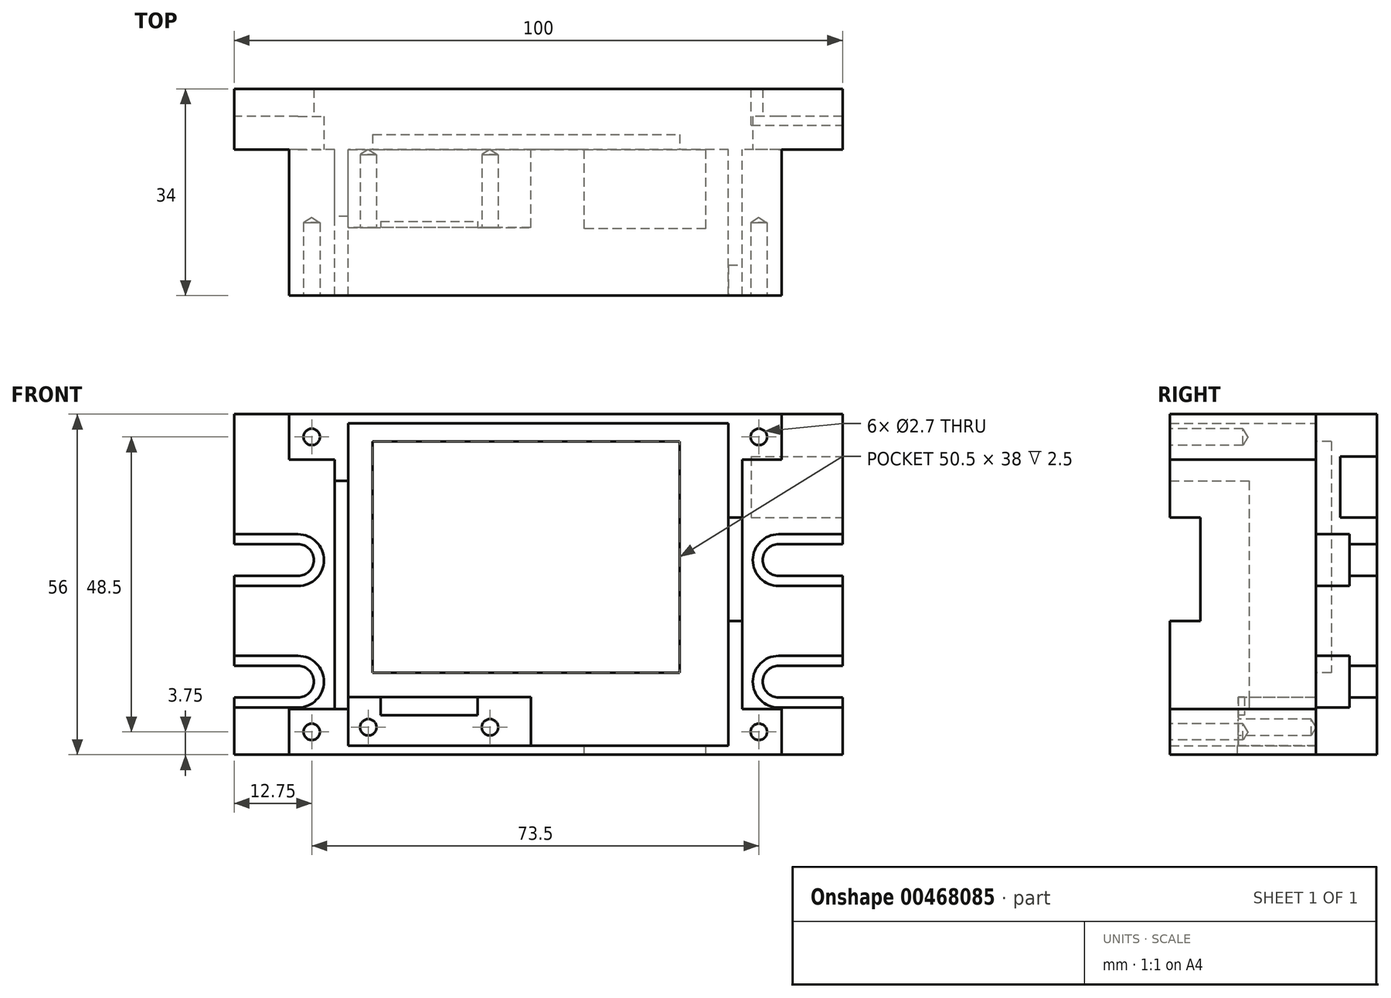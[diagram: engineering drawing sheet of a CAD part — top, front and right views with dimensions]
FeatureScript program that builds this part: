
annotation { "Feature Type Name" : "Feature", "Feature Type Description" : "" }
export const myFeature = defineFeature(function(context is Context, id is Id, definition is map)
    precondition{}
    {
        {
            var Q0;
            Q0=qCreatedBy(makeId("Front.planeOp"),FACE);
            var sketch = newSketch(context, id + "F0", { "sketchPlane" : qUnion([Q0])});
            skLineSegment(sketch, "E0", {"start": v(-65, 0) * mm, "end": v(-65, 5) * mm});
            skLineSegment(sketch, "E1", {"start": v(-65, 5) * mm, "end": v(-50, 5) * mm});
            skLineSegment(sketch, "E2", {"start": v(-50, 5) * mm, "end": v(-50, 61) * mm});
            skLineSegment(sketch, "E3", {"start": v(-50, 61) * mm, "end": v(50, 61) * mm});
            skLineSegment(sketch, "E4", {"start": v(50, 61) * mm, "end": v(50, 5) * mm});
            skLineSegment(sketch, "E5", {"start": v(50, 5) * mm, "end": v(65, 5) * mm});
            skLineSegment(sketch, "E6", {"start": v(65, 5) * mm, "end": v(65, 0) * mm});
            skLineSegment(sketch, "E7", {"start": v(65, 0) * mm, "end": v(-65, 0) * mm});
            skLineSegment(sketch, "E8", {"start": v(-66.2, 33) * mm, "end": v(67.97, 33) * mm, "construction": true});
            skLineSegment(sketch, "E9.bottom", {"start": v(-38, 45.5) * mm, "end": v(38, 45.5) * mm, "construction": true});
            skLineSegment(sketch, "E9.top", {"start": v(-38, 20.5) * mm, "end": v(38, 20.5) * mm, "construction": true});
            skLineSegment(sketch, "E9.left", {"start": v(-38, 45.5) * mm, "end": v(-38, 20.5) * mm, "construction": true});
            skLineSegment(sketch, "E9.right", {"start": v(38, 45.5) * mm, "end": v(38, 20.5) * mm, "construction": true});
            skSolve(sketch);
        }
        {
            var Q0;
            Q0=qSketchRegion(id+"F0",true);
            extrude(context, id + "F1", {"entities" : qUnion([Q0]), "depth" : 12 * mm});
        }
        {
            var Q0;
            Q0=makeQuery(id+"F1.opExtrude","SWEPT_FACE",FACE,{"disambiguationData":[OSD([sQuery(id+"F0.wireOp",EDGE,"E7")])]});
            var sketch = newSketch(context, id + "F2", { "sketchPlane" : qUnion([Q0])});
            skLineSegment(sketch, "E10", {"start": v(-65, 6) * mm, "end": v(65, 6) * mm, "construction": true});
            skArc(sketch, "E11", {"start": v(-63, 2.65) * mm, "mid": v(-59.65, 6) * mm, "end": v(-63, 9.35) * mm});
            skArc(sketch, "E12", {"start": v(63, 9.35) * mm, "mid": v(59.65, 6) * mm, "end": v(63, 2.65) * mm});
            skLineSegment(sketch, "E13", {"start": v(-63, 9.35) * mm, "end": v(-65, 9.35) * mm});
            skLineSegment(sketch, "E14", {"start": v(-63, 2.65) * mm, "end": v(-65, 2.65) * mm});
            skLineSegment(sketch, "E15", {"start": v(-65, 9.35) * mm, "end": v(-65, 2.65) * mm});
            skLineSegment(sketch, "E16", {"start": v(63, 9.35) * mm, "end": v(65, 9.35) * mm});
            skLineSegment(sketch, "E17", {"start": v(63, 2.65) * mm, "end": v(65, 2.65) * mm});
            skLineSegment(sketch, "E18", {"start": v(65, 2.65) * mm, "end": v(65, 9.35) * mm});
            skSolve(sketch);
        }
        {
            var Q0;
            Q0=qSketchRegion(id+"F2",true);
            extrude(context, id + "F3", {"entities" : qUnion([Q0]), "operationType" : NewBodyOperationType.REMOVE, "endBound" : BoundingType.UP_TO_NEXT, "oppositeDirection" : true, "depth" : 25 * mm});
        }
        {
            var Q0;
            Q0=makeQuery(id+"F1.opExtrude","CAP_FACE",FACE,{"disambiguationData":[OSD([sQuery(id+"F0.wireOp",EDGE,"E0"),sQuery(id+"F0.wireOp",EDGE,"E1"),sQuery(id+"F0.wireOp",EDGE,"E2"),sQuery(id+"F0.wireOp",EDGE,"E3"),sQuery(id+"F0.wireOp",EDGE,"E4"),sQuery(id+"F0.wireOp",EDGE,"E5"),sQuery(id+"F0.wireOp",EDGE,"E6"),sQuery(id+"F0.wireOp",EDGE,"E7"),sQuery(id+"F0.wireOp",EDGE,"1FfViyJT-DljK-amIZ-o1TR-3zgzdxAZsou7"),sQuery(id+"F0.wireOp",EDGE,"gixynyuw-ZIOC-nsWz-2FFo-MeVdqOtkgReW"),sQuery(id+"F0.wireOp",EDGE,"ZI2TBTUG-xJa5-HuRL-xrIj-cNeYduNTSZAt"),sQuery(id+"F0.wireOp",EDGE,"0vhO7cF5-ESn1-LKnd-qrl0-O6yNl9EkdQ3n")])],"isStart":true});
            var sketch = newSketch(context, id + "F4", { "sketchPlane" : qUnion([Q0])});
            skLineSegment(sketch, "E19.bottom", {"start": v(50, 5) * mm, "end": v(-50, 5) * mm});
            skLineSegment(sketch, "E19.top", {"start": v(50, 61) * mm, "end": v(-50, 61) * mm});
            skLineSegment(sketch, "E19.left", {"start": v(50, 5) * mm, "end": v(50, 61) * mm});
            skLineSegment(sketch, "E19.right", {"start": v(-50, 5) * mm, "end": v(-50, 61) * mm});
            skSolve(sketch);
        }
        {
            var Q0;
            Q0=qSketchRegion(id+"F4",true);
            extrude(context, id + "F5", {"entities" : qUnion([Q0]), "operationType" : NewBodyOperationType.REMOVE, "oppositeDirection" : true, "depth" : 2 * mm});
        }
        {
            var Q0;
            Q0=makeQuery(id+"F1.opExtrude","CAP_FACE",FACE,{"disambiguationData":[OSD([sQuery(id+"F0.wireOp",EDGE,"E0"),sQuery(id+"F0.wireOp",EDGE,"E1"),sQuery(id+"F0.wireOp",EDGE,"E2"),sQuery(id+"F0.wireOp",EDGE,"E3"),sQuery(id+"F0.wireOp",EDGE,"E4"),sQuery(id+"F0.wireOp",EDGE,"E5"),sQuery(id+"F0.wireOp",EDGE,"E6"),sQuery(id+"F0.wireOp",EDGE,"E7"),sQuery(id+"F0.wireOp",EDGE,"1FfViyJT-DljK-amIZ-o1TR-3zgzdxAZsou7"),sQuery(id+"F0.wireOp",EDGE,"gixynyuw-ZIOC-nsWz-2FFo-MeVdqOtkgReW"),sQuery(id+"F0.wireOp",EDGE,"ZI2TBTUG-xJa5-HuRL-xrIj-cNeYduNTSZAt"),sQuery(id+"F0.wireOp",EDGE,"0vhO7cF5-ESn1-LKnd-qrl0-O6yNl9EkdQ3n")])],"isStart":true});
            var sketch = newSketch(context, id + "F6", { "sketchPlane" : qUnion([Q0])});
            skLineSegment(sketch, "E20.bottom", {"start": v(65, 5) * mm, "end": v(-65, 5) * mm});
            skLineSegment(sketch, "E20.top", {"start": v(65, 0) * mm, "end": v(-65, 0) * mm});
            skLineSegment(sketch, "E20.left", {"start": v(65, 5) * mm, "end": v(65, 0) * mm});
            skLineSegment(sketch, "E20.right", {"start": v(-65, 5) * mm, "end": v(-65, 0) * mm});
            skSolve(sketch);
        }
        {
            var Q0;
            Q0=qSketchRegion(id+"F6",true);
            extrude(context, id + "F7", {"entities" : qUnion([Q0]), "operationType" : NewBodyOperationType.REMOVE, "endBound" : BoundingType.THROUGH_ALL, "oppositeDirection" : true, "depth" : 25 * mm});
        }
        {
            var Q0;
            Q0=makeQuery(id+"F1.opExtrude","CAP_FACE",FACE,{"disambiguationData":[OSD([sQuery(id+"F0.wireOp",EDGE,"E0"),sQuery(id+"F0.wireOp",EDGE,"E1"),sQuery(id+"F0.wireOp",EDGE,"E2"),sQuery(id+"F0.wireOp",EDGE,"E3"),sQuery(id+"F0.wireOp",EDGE,"E4"),sQuery(id+"F0.wireOp",EDGE,"E5"),sQuery(id+"F0.wireOp",EDGE,"E6"),sQuery(id+"F0.wireOp",EDGE,"E7"),sQuery(id+"F0.wireOp",EDGE,"1FfViyJT-DljK-amIZ-o1TR-3zgzdxAZsou7"),sQuery(id+"F0.wireOp",EDGE,"gixynyuw-ZIOC-nsWz-2FFo-MeVdqOtkgReW"),sQuery(id+"F0.wireOp",EDGE,"ZI2TBTUG-xJa5-HuRL-xrIj-cNeYduNTSZAt"),sQuery(id+"F0.wireOp",EDGE,"0vhO7cF5-ESn1-LKnd-qrl0-O6yNl9EkdQ3n")])],"isStart":false});
            var sketch = newSketch(context, id + "F8", { "sketchPlane" : qUnion([Q0])});
            skLineSegment(sketch, "E21.bottom", {"start": v(-52.5, 6) * mm, "end": v(52.5, 6) * mm, "construction": true});
            skLineSegment(sketch, "E21.top", {"start": v(-52.5, 60) * mm, "end": v(52.5, 60) * mm, "construction": true});
            skLineSegment(sketch, "E21.left", {"start": v(-52.5, 6) * mm, "end": v(-52.5, 60) * mm, "construction": true});
            skLineSegment(sketch, "E21.right", {"start": v(52.5, 6) * mm, "end": v(52.5, 60) * mm, "construction": true});
            skLineSegment(sketch, "E22", {"start": v(-65.76, 33) * mm, "end": v(79.5, 33) * mm, "construction": true});
            skArc(sketch, "E23.MirrorCS", {"start": v(-39.5, 39.6) * mm, "mid": v(-36.9, 37) * mm, "end": v(-39.5, 34.4) * mm});
            skLineSegment(sketch, "E24", {"start": v(0, 73.09) * mm, "end": v(0, -19.71) * mm, "construction": true});
            skPoint(sketch, "E24.startSnap0", {"position": v(0, 61) * mm});
            skLineSegment(sketch, "E25", {"start": v(-39.5, 39.6) * mm, "end": v(-50, 39.6) * mm});
            skLineSegment(sketch, "E26", {"start": v(-50, 39.6) * mm, "end": v(-50, 34.4) * mm});
            skLineSegment(sketch, "E27", {"start": v(-50, 34.4) * mm, "end": v(-39.5, 34.4) * mm});
            skLineSegment(sketch, "E28.0.1.0", {"start": v(-50, 19.6) * mm, "end": v(-50, 14.4) * mm});
            skLineSegment(sketch, "E28.0.1.1", {"start": v(-50, 14.4) * mm, "end": v(-39.5, 14.4) * mm});
            skLineSegment(sketch, "E28.0.1.2", {"start": v(-39.5, 19.6) * mm, "end": v(-50, 19.6) * mm});
            skArc(sketch, "E28.0.1.3", {"start": v(-39.5, 19.6) * mm, "mid": v(-36.9, 17) * mm, "end": v(-39.5, 14.4) * mm});
            skLineSegment(sketch, "E28.direction1", {"start": v(-50, 34.4) * mm, "end": v(-25, 34.4) * mm, "construction": true});
            skLineSegment(sketch, "E28.direction2", {"start": v(-50, 34.4) * mm, "end": v(-50, 14.4) * mm, "construction": true});
            skArc(sketch, "E29.MirrorCS", {"start": v(39.5, 39.6) * mm, "mid": v(36.9, 37) * mm, "end": v(39.5, 34.4) * mm});
            skLineSegment(sketch, "E30.MirrorCS", {"start": v(50, 39.6) * mm, "end": v(50, 34.4) * mm});
            skLineSegment(sketch, "E31.MirrorCS", {"start": v(50, 19.6) * mm, "end": v(50, 14.4) * mm});
            skArc(sketch, "E32.MirrorCS", {"start": v(39.5, 19.6) * mm, "mid": v(36.9, 17) * mm, "end": v(39.5, 14.4) * mm});
            skLineSegment(sketch, "E33.MirrorCS", {"start": v(50, 34.4) * mm, "end": v(39.5, 34.4) * mm});
            skLineSegment(sketch, "E34.MirrorCS", {"start": v(50, 34.4) * mm, "end": v(50, 14.4) * mm, "construction": true});
            skLineSegment(sketch, "E35.MirrorCS", {"start": v(50, 34.4) * mm, "end": v(25, 34.4) * mm, "construction": true});
            skLineSegment(sketch, "E36.MirrorCS", {"start": v(39.5, 39.6) * mm, "end": v(50, 39.6) * mm});
            skLineSegment(sketch, "E37.MirrorCS", {"start": v(50, 14.4) * mm, "end": v(39.5, 14.4) * mm});
            skLineSegment(sketch, "E38.MirrorCS", {"start": v(39.5, 19.6) * mm, "end": v(50, 19.6) * mm});
            skSolve(sketch);
        }
        {
            var Q0;
            Q0=qSketchRegion(id+"F8",true);
            extrude(context, id + "F9", {"entities" : qUnion([Q0]), "operationType" : NewBodyOperationType.REMOVE, "endBound" : BoundingType.THROUGH_ALL, "oppositeDirection" : true, "depth" : 25 * mm});
        }
        {
            var Q0;
            Q0=makeQuery(id+"F1.opExtrude","CAP_FACE",FACE,{"disambiguationData":[OSD([sQuery(id+"F0.wireOp",EDGE,"E0"),sQuery(id+"F0.wireOp",EDGE,"E1"),sQuery(id+"F0.wireOp",EDGE,"E2"),sQuery(id+"F0.wireOp",EDGE,"E3"),sQuery(id+"F0.wireOp",EDGE,"E4"),sQuery(id+"F0.wireOp",EDGE,"E5"),sQuery(id+"F0.wireOp",EDGE,"E6"),sQuery(id+"F0.wireOp",EDGE,"E7"),sQuery(id+"F0.wireOp",EDGE,"1FfViyJT-DljK-amIZ-o1TR-3zgzdxAZsou7"),sQuery(id+"F0.wireOp",EDGE,"gixynyuw-ZIOC-nsWz-2FFo-MeVdqOtkgReW"),sQuery(id+"F0.wireOp",EDGE,"ZI2TBTUG-xJa5-HuRL-xrIj-cNeYduNTSZAt"),sQuery(id+"F0.wireOp",EDGE,"0vhO7cF5-ESn1-LKnd-qrl0-O6yNl9EkdQ3n")])],"isStart":false});
            var sketch = newSketch(context, id + "F10", { "sketchPlane" : qUnion([Q0])});
            skArc(sketch, "E39", {"start": v(-39.5, 32.75) * mm, "mid": v(-35.25, 37) * mm, "end": v(-39.5, 41.25) * mm});
            skLineSegment(sketch, "E40", {"start": v(-39.5, 41.25) * mm, "end": v(-50, 41.25) * mm});
            skLineSegment(sketch, "E41", {"start": v(-39.5, 32.75) * mm, "end": v(-50, 32.75) * mm});
            skLineSegment(sketch, "E42", {"start": v(0, 67.71) * mm, "end": v(0, -2.74) * mm, "construction": true});
            skPoint(sketch, "E42.startSnap0", {"position": v(0, 61) * mm});
            skLineSegment(sketch, "E43.0.1.0", {"start": v(-39.5, 12.75) * mm, "end": v(-50, 12.75) * mm});
            skLineSegment(sketch, "E43.0.1.1", {"start": v(-39.5, 21.25) * mm, "end": v(-50, 21.25) * mm});
            skArc(sketch, "E43.0.1.2", {"start": v(-39.5, 12.75) * mm, "mid": v(-35.25, 17) * mm, "end": v(-39.5, 21.25) * mm});
            skLineSegment(sketch, "E43.direction1", {"start": v(-50, 32.75) * mm, "end": v(-25, 32.75) * mm, "construction": true});
            skLineSegment(sketch, "E43.direction2", {"start": v(-50, 32.75) * mm, "end": v(-50, 12.75) * mm, "construction": true});
            skLineSegment(sketch, "E44.MirrorCS", {"start": v(39.5, 32.75) * mm, "end": v(50, 32.75) * mm});
            skLineSegment(sketch, "E45.MirrorCS", {"start": v(50, 32.75) * mm, "end": v(50, 12.75) * mm, "construction": true});
            skLineSegment(sketch, "E46.MirrorCS", {"start": v(39.5, 21.25) * mm, "end": v(50, 21.25) * mm});
            skLineSegment(sketch, "E47.MirrorCS", {"start": v(39.5, 12.75) * mm, "end": v(50, 12.75) * mm});
            skArc(sketch, "E48.MirrorCS", {"start": v(39.5, 12.75) * mm, "mid": v(35.25, 17) * mm, "end": v(39.5, 21.25) * mm});
            skArc(sketch, "E49.MirrorCS", {"start": v(39.5, 32.75) * mm, "mid": v(35.25, 37) * mm, "end": v(39.5, 41.25) * mm});
            skLineSegment(sketch, "E50.MirrorCS", {"start": v(39.5, 41.25) * mm, "end": v(50, 41.25) * mm});
            skLineSegment(sketch, "E51.MirrorCS", {"start": v(50, 32.75) * mm, "end": v(25, 32.75) * mm, "construction": true});
            skSolve(sketch);
        }
        {
            var Q0;
            Q0=makeQuery(id+"F10.imprint","IMPRINT",FACE,{"disambiguationData":[TD([[makeQuery(id+"F10.imprint","IMPRINT",EDGE,{"derivedFrom":sQuery(id+"F10.wireOp",EDGE,"E39")}),1.0]])]});
            var Q1;
            {var subQ3=sQuery(id+"F10.wireOp",EDGE,"E43.0.1.0");Q1=makeQuery(id+"F10.imprint","IMPRINT",FACE,{"disambiguationData":[TD([[makeQuery(id+"F10.imprint","IMPRINT",EDGE,{"derivedFrom":subQ3}),-1.0]])]});}
            var Q2;
            {var subQ3=sQuery(id+"F10.wireOp",EDGE,"E44.MirrorCS");Q2=makeQuery(id+"F10.imprint","IMPRINT",FACE,{"disambiguationData":[TD([[makeQuery(id+"F10.imprint","IMPRINT",EDGE,{"derivedFrom":subQ3}),1.0]])]});}
            var Q3;
            {var subQ1=sQuery(id+"F10.wireOp",EDGE,"E46.MirrorCS");Q3=makeQuery(id+"F10.imprint","IMPRINT",FACE,{"disambiguationData":[TD([[makeQuery(id+"F10.imprint","IMPRINT",EDGE,{"derivedFrom":subQ1}),-1.0]])]});}
            extrude(context, id + "F11", {"entities" : qUnion([Q0, Q1, Q2, Q3]), "operationType" : NewBodyOperationType.REMOVE, "oppositeDirection" : true, "depth" : 5.5 * mm});
        }
        {
            var Q0;
            Q0=makeQuery(id+"F1.opExtrude","CAP_FACE",FACE,{"disambiguationData":[OSD([sQuery(id+"F0.wireOp",EDGE,"E0"),sQuery(id+"F0.wireOp",EDGE,"E1"),sQuery(id+"F0.wireOp",EDGE,"E2"),sQuery(id+"F0.wireOp",EDGE,"E3"),sQuery(id+"F0.wireOp",EDGE,"E4"),sQuery(id+"F0.wireOp",EDGE,"E5"),sQuery(id+"F0.wireOp",EDGE,"E6"),sQuery(id+"F0.wireOp",EDGE,"E7"),sQuery(id+"F0.wireOp",EDGE,"1FfViyJT-DljK-amIZ-o1TR-3zgzdxAZsou7"),sQuery(id+"F0.wireOp",EDGE,"gixynyuw-ZIOC-nsWz-2FFo-MeVdqOtkgReW"),sQuery(id+"F0.wireOp",EDGE,"ZI2TBTUG-xJa5-HuRL-xrIj-cNeYduNTSZAt"),sQuery(id+"F0.wireOp",EDGE,"0vhO7cF5-ESn1-LKnd-qrl0-O6yNl9EkdQ3n")])],"isStart":false});
            var sketch = newSketch(context, id + "F12", { "sketchPlane" : qUnion([Q0])});
            skLineSegment(sketch, "E52", {"start": v(-67.67, 33) * mm, "end": v(65.75, 33) * mm, "construction": true});
            skPoint(sketch, "E52.startSnap0", {"position": v(-50, 33) * mm});
            skLineSegment(sketch, "E53", {"start": v(0, 70.32) * mm, "end": v(0, -7.36) * mm, "construction": true});
            skPoint(sketch, "E53.startSnap0", {"position": v(0, 61) * mm});
            skLineSegment(sketch, "E54.bottom", {"start": v(31.25, 59.5) * mm, "end": v(-31.25, 59.5) * mm});
            skLineSegment(sketch, "E54.top", {"start": v(31.25, 6.5) * mm, "end": v(-31.25, 6.5) * mm});
            skLineSegment(sketch, "E54.left", {"start": v(31.25, 59.5) * mm, "end": v(31.25, 6.5) * mm});
            skLineSegment(sketch, "E54.right", {"start": v(-31.25, 59.5) * mm, "end": v(-31.25, 6.5) * mm});
            skPoint(sketch, "E54.middle", {"position": v(0, 33) * mm});
            skLineSegment(sketch, "E55.bottom", {"start": v(33.5, 61) * mm, "end": v(-33.5, 61) * mm});
            skLineSegment(sketch, "E55.top", {"start": v(33.5, 5) * mm, "end": v(-33.5, 5) * mm});
            skLineSegment(sketch, "E55.left", {"start": v(33.5, 61) * mm, "end": v(33.5, 5) * mm});
            skLineSegment(sketch, "E55.right", {"start": v(-33.5, 61) * mm, "end": v(-33.5, 5) * mm});
            skSolve(sketch);
        }
        {
            var Q0;
            Q0=makeQuery(id+"F12.imprint","IMPRINT",FACE,{"disambiguationData":[TD([[makeQuery(id+"F12.imprint","IMPRINT",EDGE,{"derivedFrom":sQuery(id+"F12.wireOp",EDGE,"E54.bottom")}),-1.0]])]});
            extrude(context, id + "F13", {"entities" : qUnion([Q0]), "operationType" : NewBodyOperationType.ADD, "depth" : 24 * mm});
        }
        {
            var Q0;
            Q0=makeQuery(id+"F13.boolean.opBoolean","SPLIT",FACE,{"disambiguationData":[TD([makeQuery(id+"F13.opExtrude","SWEPT_FACE",FACE,{"disambiguationData":[OSD([sQuery(id+"F12.wireOp",EDGE,"E54.bottom")])]})])],"derivedFrom":makeQuery(id+"F1.opExtrude","CAP_FACE",FACE,{"disambiguationData":[OSD([sQuery(id+"F0.wireOp",EDGE,"E0"),sQuery(id+"F0.wireOp",EDGE,"E1"),sQuery(id+"F0.wireOp",EDGE,"E2"),sQuery(id+"F0.wireOp",EDGE,"E3"),sQuery(id+"F0.wireOp",EDGE,"E4"),sQuery(id+"F0.wireOp",EDGE,"E5"),sQuery(id+"F0.wireOp",EDGE,"E6"),sQuery(id+"F0.wireOp",EDGE,"E7"),sQuery(id+"F0.wireOp",EDGE,"1FfViyJT-DljK-amIZ-o1TR-3zgzdxAZsou7"),sQuery(id+"F0.wireOp",EDGE,"gixynyuw-ZIOC-nsWz-2FFo-MeVdqOtkgReW"),sQuery(id+"F0.wireOp",EDGE,"ZI2TBTUG-xJa5-HuRL-xrIj-cNeYduNTSZAt"),sQuery(id+"F0.wireOp",EDGE,"0vhO7cF5-ESn1-LKnd-qrl0-O6yNl9EkdQ3n")])],"isStart":false})});
            var sketch = newSketch(context, id + "F14", { "sketchPlane" : qUnion([Q0])});
            skLineSegment(sketch, "E56.bottom", {"start": v(-31.25, 6.5) * mm, "end": v(-1.25, 6.5) * mm});
            skLineSegment(sketch, "E56.top", {"start": v(-31.25, 14.5) * mm, "end": v(-1.25, 14.5) * mm});
            skLineSegment(sketch, "E56.left", {"start": v(-31.25, 6.5) * mm, "end": v(-31.25, 14.5) * mm});
            skLineSegment(sketch, "E56.right", {"start": v(-1.25, 6.5) * mm, "end": v(-1.25, 14.5) * mm});
            skSolve(sketch);
        }
        {
            var Q0;
            Q0=makeQuery(id+"F14.imprint","IMPRINT",FACE,{"disambiguationData":[TD([[makeQuery(id+"F14.imprint","IMPRINT",EDGE,{"derivedFrom":sQuery(id+"F14.wireOp",EDGE,"E56.bottom")}),-1.0]])]});
            extrude(context, id + "F15", {"entities" : qUnion([Q0]), "operationType" : NewBodyOperationType.ADD, "depth" : 12.8 * mm});
        }
        {
            var Q0;
            Q0=makeQuery(id+"F13.opExtrude","SWEPT_FACE",FACE,{"disambiguationData":[OSD([sQuery(id+"F12.wireOp",EDGE,"E55.right")])]});
            var sketch = newSketch(context, id + "F16", { "sketchPlane" : qUnion([Q0])});
            skLineSegment(sketch, "E57.bottom", {"start": v(36, 50) * mm, "end": v(23, 50) * mm});
            skLineSegment(sketch, "E57.top", {"start": v(36, 12.5) * mm, "end": v(23, 12.5) * mm});
            skLineSegment(sketch, "E57.left", {"start": v(36, 50) * mm, "end": v(36, 12.5) * mm});
            skLineSegment(sketch, "E57.right", {"start": v(23, 50) * mm, "end": v(23, 12.5) * mm});
            skSolve(sketch);
        }
        {
            var Q0;
            Q0=makeQuery(id+"F16.imprint","IMPRINT",FACE,{"disambiguationData":[TD([[makeQuery(id+"F16.imprint","IMPRINT",EDGE,{"derivedFrom":sQuery(id+"F16.wireOp",EDGE,"E57.bottom")}),1.0]])]});
            var Q1;
            Q1=makeQuery(id+"F13.opExtrude","SWEPT_FACE",FACE,{"disambiguationData":[OSD([sQuery(id+"F12.wireOp",EDGE,"E54.right")])]});
            extrude(context, id + "F17", {"entities" : qUnion([Q0]), "operationType" : NewBodyOperationType.REMOVE, "endBound" : BoundingType.UP_TO_SURFACE, "oppositeDirection" : true, "endBoundEntityFace" : qUnion([Q1]), "depth" : 25 * mm});
        }
        {
            var Q0;
            Q0=makeQuery(id+"F13.boolean.opBoolean","MERGE",FACE,{"derivedFrom":[makeQuery(id+"F7.boolean.opBoolean","COPY",FACE,{"derivedFrom":makeQuery(id+"F7.opExtrude","SWEPT_FACE",FACE,{"disambiguationData":[OSD([sQuery(id+"F6.wireOp",EDGE,"E20.bottom")])]})}),makeQuery(id+"F13.opExtrude","SWEPT_FACE",FACE,{"disambiguationData":[OSD([sQuery(id+"F12.wireOp",EDGE,"E55.top")])]})]});
            var sketch = newSketch(context, id + "F18", { "sketchPlane" : qUnion([Q0])});
            skLineSegment(sketch, "E58.bottom", {"start": v(7.5, 25) * mm, "end": v(27.5, 25) * mm});
            skLineSegment(sketch, "E58.top", {"start": v(7.5, 12) * mm, "end": v(27.5, 12) * mm});
            skLineSegment(sketch, "E58.left", {"start": v(7.5, 25) * mm, "end": v(7.5, 12) * mm});
            skLineSegment(sketch, "E58.right", {"start": v(27.5, 25) * mm, "end": v(27.5, 12) * mm});
            skSolve(sketch);
        }
        {
            var Q0;
            Q0=makeQuery(id+"F18.imprint","IMPRINT",FACE,{"disambiguationData":[TD([[makeQuery(id+"F18.imprint","IMPRINT",EDGE,{"derivedFrom":sQuery(id+"F18.wireOp",EDGE,"E58.bottom")}),-1.0]])]});
            extrude(context, id + "F19", {"entities" : qUnion([Q0]), "operationType" : NewBodyOperationType.REMOVE, "endBound" : BoundingType.UP_TO_NEXT, "oppositeDirection" : true, "depth" : 25 * mm});
        }
        {
            var Q0;
            Q0=makeQuery(id+"F15.opExtrude","CAP_FACE",FACE,{"disambiguationData":[OSD([sQuery(id+"F14.wireOp",EDGE,"E56.bottom"),sQuery(id+"F14.wireOp",EDGE,"E56.top"),sQuery(id+"F14.wireOp",EDGE,"E56.left"),sQuery(id+"F14.wireOp",EDGE,"E56.right")])],"isStart":false});
            var sketch = newSketch(context, id + "F20", { "sketchPlane" : qUnion([Q0])});
            skPoint(sketch, "E59", {"position": v(-27.95, 9.5) * mm});
            skPoint(sketch, "E60", {"position": v(-7.95, 9.5) * mm});
            skSolve(sketch);
        }
        {
            var Q0;
            Q0=sQuery(id+"F20.wireOp",VERTEX,"E59");
            var Q1;
            Q1=sQuery(id+"F20.wireOp",VERTEX,"E60");
            var Q2;
            Q2=makeQuery(id+"F1.opExtrude","SWEPT_BODY",BODY,{"disambiguationData":[OSD([sQuery(id+"F0.wireOp",EDGE,"E0"),sQuery(id+"F0.wireOp",EDGE,"E1"),sQuery(id+"F0.wireOp",EDGE,"E2"),sQuery(id+"F0.wireOp",EDGE,"E3"),sQuery(id+"F0.wireOp",EDGE,"E4"),sQuery(id+"F0.wireOp",EDGE,"E5"),sQuery(id+"F0.wireOp",EDGE,"E6"),sQuery(id+"F0.wireOp",EDGE,"E7"),sQuery(id+"F0.wireOp",EDGE,"1FfViyJT-DljK-amIZ-o1TR-3zgzdxAZsou7"),sQuery(id+"F0.wireOp",EDGE,"gixynyuw-ZIOC-nsWz-2FFo-MeVdqOtkgReW"),sQuery(id+"F0.wireOp",EDGE,"ZI2TBTUG-xJa5-HuRL-xrIj-cNeYduNTSZAt"),sQuery(id+"F0.wireOp",EDGE,"0vhO7cF5-ESn1-LKnd-qrl0-O6yNl9EkdQ3n")])]});
            hole(context, id + "F21", {"style" : HoleStyle.SIMPLE, "endStyle" : HoleEndStyle.BLIND, "holeDiameter" : 2.7 * mm, "holeDepth" : 12 * mm, "isTappedThrough" : true, "tappedDepth" : 12 * mm, "tapClearance" : 3, "startFromSketch" : true, "locations" : qUnion([Q0, Q1]), "scope" : qUnion([Q2])});
        }
        {
            var Q0;
            Q0=makeQuery(id+"F19.boolean.opBoolean","MERGE",FACE,{"derivedFrom":[makeQuery(id+"F13.boolean.opBoolean","SPLIT",FACE,{"disambiguationData":[TD([makeQuery(id+"F13.opExtrude","SWEPT_FACE",FACE,{"disambiguationData":[OSD([sQuery(id+"F12.wireOp",EDGE,"E54.bottom")])]})])],"derivedFrom":makeQuery(id+"F1.opExtrude","CAP_FACE",FACE,{"disambiguationData":[OSD([sQuery(id+"F0.wireOp",EDGE,"E0"),sQuery(id+"F0.wireOp",EDGE,"E1"),sQuery(id+"F0.wireOp",EDGE,"E2"),sQuery(id+"F0.wireOp",EDGE,"E3"),sQuery(id+"F0.wireOp",EDGE,"E4"),sQuery(id+"F0.wireOp",EDGE,"E5"),sQuery(id+"F0.wireOp",EDGE,"E6"),sQuery(id+"F0.wireOp",EDGE,"E7"),sQuery(id+"F0.wireOp",EDGE,"1FfViyJT-DljK-amIZ-o1TR-3zgzdxAZsou7"),sQuery(id+"F0.wireOp",EDGE,"gixynyuw-ZIOC-nsWz-2FFo-MeVdqOtkgReW"),sQuery(id+"F0.wireOp",EDGE,"ZI2TBTUG-xJa5-HuRL-xrIj-cNeYduNTSZAt"),sQuery(id+"F0.wireOp",EDGE,"0vhO7cF5-ESn1-LKnd-qrl0-O6yNl9EkdQ3n")])],"isStart":false})}),makeQuery(id+"F19.opExtrude","SWEPT_FACE",FACE,{"disambiguationData":[OSD([sQuery(id+"F18.wireOp",EDGE,"E58.top")])]})]});
            var sketch = newSketch(context, id + "F22", { "sketchPlane" : qUnion([Q0])});
            skLineSegment(sketch, "E61.bottom", {"start": v(-27.25, 56.5) * mm, "end": v(23.25, 56.5) * mm});
            skLineSegment(sketch, "E61.top", {"start": v(-27.25, 18.5) * mm, "end": v(23.25, 18.5) * mm});
            skLineSegment(sketch, "E61.left", {"start": v(-27.25, 56.5) * mm, "end": v(-27.25, 18.5) * mm});
            skLineSegment(sketch, "E61.right", {"start": v(23.25, 56.5) * mm, "end": v(23.25, 18.5) * mm});
            skSolve(sketch);
        }
        {
            var Q0;
            Q0=makeQuery(id+"F22.imprint","IMPRINT",FACE,{"disambiguationData":[TD([[makeQuery(id+"F22.imprint","IMPRINT",EDGE,{"derivedFrom":sQuery(id+"F22.wireOp",EDGE,"E61.bottom")}),-1.0]])]});
            extrude(context, id + "F23", {"entities" : qUnion([Q0]), "operationType" : NewBodyOperationType.REMOVE, "oppositeDirection" : true, "depth" : 2.5 * mm});
        }
        {
            var Q0;
            {var subQ0=sQuery(id+"F0.wireOp",EDGE,"E3");var subQ1=sQuery(id+"F0.wireOp",EDGE,"E2");var subQ2=sQuery(id+"F0.wireOp",EDGE,"1FfViyJT-DljK-amIZ-o1TR-3zgzdxAZsou7");var subQ3=sQuery(id+"F0.wireOp",EDGE,"E1");var subQ4=sQuery(id+"F0.wireOp",EDGE,"ZI2TBTUG-xJa5-HuRL-xrIj-cNeYduNTSZAt");Q0=makeQuery(id+"F13.boolean.opBoolean","SPLIT",FACE,{"disambiguationData":[TD([makeQuery(id+"F1.opExtrude","SWEPT_FACE",FACE,{"disambiguationData":[OSD([subQ1])]})])],"derivedFrom":makeQuery(id+"F1.opExtrude","CAP_FACE",FACE,{"disambiguationData":[OSD([sQuery(id+"F0.wireOp",EDGE,"E0"),subQ3,subQ1,subQ0,sQuery(id+"F0.wireOp",EDGE,"E4"),sQuery(id+"F0.wireOp",EDGE,"E5"),sQuery(id+"F0.wireOp",EDGE,"E6"),sQuery(id+"F0.wireOp",EDGE,"E7"),subQ2,sQuery(id+"F0.wireOp",EDGE,"gixynyuw-ZIOC-nsWz-2FFo-MeVdqOtkgReW"),subQ4,sQuery(id+"F0.wireOp",EDGE,"0vhO7cF5-ESn1-LKnd-qrl0-O6yNl9EkdQ3n")])],"isStart":false})});}
            var sketch = newSketch(context, id + "F24", { "sketchPlane" : qUnion([Q0])});
            skLineSegment(sketch, "E62.bottom", {"start": v(-33.5, 5) * mm, "end": v(-41, 5) * mm});
            skLineSegment(sketch, "E62.top", {"start": v(-33.5, 12.5) * mm, "end": v(-41, 12.5) * mm});
            skLineSegment(sketch, "E62.left", {"start": v(-33.5, 5) * mm, "end": v(-33.5, 12.5) * mm});
            skLineSegment(sketch, "E62.right", {"start": v(-41, 5) * mm, "end": v(-41, 12.5) * mm});
            skLineSegment(sketch, "E63.2.0.0", {"start": v(114, 12.5) * mm, "end": v(106.5, 12.5) * mm});
            skLineSegment(sketch, "E63.2.0.1", {"start": v(106.5, 5) * mm, "end": v(106.5, 12.5) * mm});
            skLineSegment(sketch, "E63.2.0.2", {"start": v(114, 5) * mm, "end": v(106.5, 5) * mm});
            skLineSegment(sketch, "E63.2.0.3", {"start": v(114, 5) * mm, "end": v(114, 12.5) * mm});
            skLineSegment(sketch, "E64.0.1.0", {"start": v(-33.5, 53.5) * mm, "end": v(-41, 53.5) * mm});
            skLineSegment(sketch, "E64.0.1.1", {"start": v(-33.5, 53.5) * mm, "end": v(-33.5, 61) * mm});
            skLineSegment(sketch, "E64.0.1.2", {"start": v(-33.5, 61) * mm, "end": v(-41, 61) * mm});
            skLineSegment(sketch, "E64.0.1.3", {"start": v(-41, 53.5) * mm, "end": v(-41, 61) * mm});
            skLineSegment(sketch, "E64.1.0.0", {"start": v(40, 5) * mm, "end": v(32.5, 5) * mm});
            skLineSegment(sketch, "E64.1.0.1", {"start": v(40, 5) * mm, "end": v(40, 12.5) * mm});
            skLineSegment(sketch, "E64.1.0.2", {"start": v(40, 12.5) * mm, "end": v(32.5, 12.5) * mm});
            skLineSegment(sketch, "E64.1.0.3", {"start": v(32.5, 5) * mm, "end": v(32.5, 12.5) * mm});
            skLineSegment(sketch, "E64.1.1.0", {"start": v(40, 53.5) * mm, "end": v(32.5, 53.5) * mm});
            skLineSegment(sketch, "E64.1.1.1", {"start": v(40, 53.5) * mm, "end": v(40, 61) * mm});
            skLineSegment(sketch, "E64.1.1.2", {"start": v(40, 61) * mm, "end": v(32.5, 61) * mm});
            skLineSegment(sketch, "E64.1.1.3", {"start": v(32.5, 53.5) * mm, "end": v(32.5, 61) * mm});
            skLineSegment(sketch, "E64.direction1", {"start": v(-41, 5) * mm, "end": v(32.5, 5) * mm, "construction": true});
            skLineSegment(sketch, "E64.direction2", {"start": v(-41, 5) * mm, "end": v(-41, 53.5) * mm, "construction": true});
            skSolve(sketch);
        }
        {
            var Q0;
            Q0=makeQuery(id+"F24.imprint","IMPRINT",FACE,{"disambiguationData":[TD([[makeQuery(id+"F24.imprint","IMPRINT",EDGE,{"derivedFrom":sQuery(id+"F24.wireOp",EDGE,"E64.1.1.0")}),-1.0]])]});
            var Q1;
            Q1=makeQuery(id+"F24.imprint","IMPRINT",FACE,{"disambiguationData":[TD([[makeQuery(id+"F24.imprint","IMPRINT",EDGE,{"derivedFrom":sQuery(id+"F24.wireOp",EDGE,"E64.1.0.0")}),-1.0]])]});
            var Q2;
            Q2=makeQuery(id+"F24.imprint","IMPRINT",FACE,{"disambiguationData":[TD([[makeQuery(id+"F24.imprint","IMPRINT",EDGE,{"derivedFrom":sQuery(id+"F24.wireOp",EDGE,"E62.bottom")}),-1.0]])]});
            var Q3;
            Q3=makeQuery(id+"F24.imprint","IMPRINT",FACE,{"disambiguationData":[TD([[makeQuery(id+"F24.imprint","IMPRINT",EDGE,{"derivedFrom":sQuery(id+"F24.wireOp",EDGE,"E64.0.1.0")}),-1.0]])]});
            var Q4;
            Q4=makeQuery(id+"F13.opExtrude","CAP_FACE",FACE,{"disambiguationData":[OSD([sQuery(id+"F12.wireOp",EDGE,"E54.bottom"),sQuery(id+"F12.wireOp",EDGE,"E54.top"),sQuery(id+"F12.wireOp",EDGE,"E54.left"),sQuery(id+"F12.wireOp",EDGE,"E54.right"),sQuery(id+"F12.wireOp",EDGE,"E55.bottom"),sQuery(id+"F12.wireOp",EDGE,"E55.top"),sQuery(id+"F12.wireOp",EDGE,"E55.left"),sQuery(id+"F12.wireOp",EDGE,"E55.right")])],"isStart":false});
            extrude(context, id + "F25", {"entities" : qUnion([Q0, Q1, Q2, Q3]), "operationType" : NewBodyOperationType.ADD, "endBound" : BoundingType.UP_TO_SURFACE, "endBoundEntityFace" : qUnion([Q4]), "depth" : 25 * mm});
        }
        {
            var Q0;
            {var subQ0=sQuery(id+"F12.wireOp",EDGE,"E55.right");var subQ1=sQuery(id+"F12.wireOp",EDGE,"E55.left");var subQ2=sQuery(id+"F12.wireOp",EDGE,"E55.top");var subQ3=sQuery(id+"F12.wireOp",EDGE,"E55.bottom");var subQ4=sQuery(id+"F12.wireOp",EDGE,"E54.right");var subQ5=sQuery(id+"F12.wireOp",EDGE,"E54.left");var subQ6=sQuery(id+"F12.wireOp",EDGE,"E54.top");var subQ7=sQuery(id+"F12.wireOp",EDGE,"E54.bottom");Q0=makeQuery(id+"F25.boolean.opBoolean","MERGE",FACE,{"derivedFrom":[makeQuery(id+"F13.opExtrude","CAP_FACE",FACE,{"disambiguationData":[OSD([subQ7,subQ6,subQ5,subQ4,subQ3,subQ2,subQ1,subQ0])],"isStart":false}),makeQuery(id+"F25.opExtrude","CAP_FACE",FACE,{"disambiguationData":[OSD([subQ7,subQ6,subQ5,subQ4,subQ3,subQ2,subQ1,subQ0]),ownerDisambiguation([makeQuery(id+"F24.imprint","IMPRINT",EDGE,{"derivedFrom":sQuery(id+"F24.wireOp",EDGE,"E62.bottom")})])],"isStart":false}),makeQuery(id+"F25.opExtrude","CAP_FACE",FACE,{"disambiguationData":[OSD([subQ7,subQ6,subQ5,subQ4,subQ3,subQ2,subQ1,subQ0]),ownerDisambiguation([makeQuery(id+"F24.imprint","IMPRINT",EDGE,{"derivedFrom":sQuery(id+"F24.wireOp",EDGE,"E64.0.1.0")})])],"isStart":false}),makeQuery(id+"F25.opExtrude","CAP_FACE",FACE,{"disambiguationData":[OSD([subQ7,subQ6,subQ5,subQ4,subQ3,subQ2,subQ1,subQ0]),ownerDisambiguation([makeQuery(id+"F24.imprint","IMPRINT",EDGE,{"derivedFrom":sQuery(id+"F24.wireOp",EDGE,"E64.1.0.0")})])],"isStart":false}),makeQuery(id+"F25.opExtrude","CAP_FACE",FACE,{"disambiguationData":[OSD([subQ7,subQ6,subQ5,subQ4,subQ3,subQ2,subQ1,subQ0]),ownerDisambiguation([makeQuery(id+"F24.imprint","IMPRINT",EDGE,{"derivedFrom":sQuery(id+"F24.wireOp",EDGE,"E64.1.1.0")})])],"isStart":false})]});}
            var sketch = newSketch(context, id + "F26", { "sketchPlane" : qUnion([Q0])});
            skPoint(sketch, "E65", {"position": v(36.25, 57.25) * mm});
            skPoint(sketch, "E66", {"position": v(36.25, 8.75) * mm});
            skPoint(sketch, "E66.positionSnap0", {"position": v(40, 8.75) * mm});
            skPoint(sketch, "E67", {"position": v(-37.25, 8.75) * mm});
            skPoint(sketch, "E67.positionSnap0", {"position": v(-41, 8.75) * mm});
            skPoint(sketch, "E68", {"position": v(-37.25, 57.25) * mm});
            skPoint(sketch, "E68.positionSnap0", {"position": v(-41, 57.25) * mm});
            skSolve(sketch);
        }
        {
            var Q0;
            Q0=sQuery(id+"F26.wireOp",VERTEX,"E65");
            var Q1;
            Q1=sQuery(id+"F26.wireOp",VERTEX,"E66");
            var Q2;
            Q2=sQuery(id+"F26.wireOp",VERTEX,"E67");
            var Q3;
            Q3=sQuery(id+"F26.wireOp",VERTEX,"E68");
            var Q4;
            Q4=makeQuery(id+"F1.opExtrude","SWEPT_BODY",BODY,{"disambiguationData":[OSD([sQuery(id+"F0.wireOp",EDGE,"E0"),sQuery(id+"F0.wireOp",EDGE,"E1"),sQuery(id+"F0.wireOp",EDGE,"E2"),sQuery(id+"F0.wireOp",EDGE,"E3"),sQuery(id+"F0.wireOp",EDGE,"E4"),sQuery(id+"F0.wireOp",EDGE,"E5"),sQuery(id+"F0.wireOp",EDGE,"E6"),sQuery(id+"F0.wireOp",EDGE,"E7"),sQuery(id+"F0.wireOp",EDGE,"1FfViyJT-DljK-amIZ-o1TR-3zgzdxAZsou7"),sQuery(id+"F0.wireOp",EDGE,"gixynyuw-ZIOC-nsWz-2FFo-MeVdqOtkgReW"),sQuery(id+"F0.wireOp",EDGE,"ZI2TBTUG-xJa5-HuRL-xrIj-cNeYduNTSZAt"),sQuery(id+"F0.wireOp",EDGE,"0vhO7cF5-ESn1-LKnd-qrl0-O6yNl9EkdQ3n")])]});
            hole(context, id + "F27", {"style" : HoleStyle.SIMPLE, "endStyle" : HoleEndStyle.BLIND, "holeDiameter" : 2.7 * mm, "holeDepth" : 12 * mm, "isTappedThrough" : true, "tappedDepth" : 12 * mm, "tapClearance" : 3, "startFromSketch" : true, "locations" : qUnion([Q0, Q1, Q2, Q3]), "scope" : qUnion([Q4])});
        }
        {
            var Q0;
            Q0=makeQuery(id+"F13.opExtrude","SWEPT_FACE",FACE,{"disambiguationData":[OSD([sQuery(id+"F12.wireOp",EDGE,"E55.left")])]});
            var sketch = newSketch(context, id + "F28", { "sketchPlane" : qUnion([Q0])});
            skLineSegment(sketch, "E69.bottom", {"start": v(-36, 27) * mm, "end": v(-31, 27) * mm});
            skLineSegment(sketch, "E69.top", {"start": v(-36, 44) * mm, "end": v(-31, 44) * mm});
            skLineSegment(sketch, "E69.left", {"start": v(-36, 27) * mm, "end": v(-36, 44) * mm});
            skLineSegment(sketch, "E69.right", {"start": v(-31, 27) * mm, "end": v(-31, 44) * mm});
            skSolve(sketch);
        }
        {
            var Q0;
            Q0=makeQuery(id+"F28.imprint","IMPRINT",FACE,{"disambiguationData":[TD([[makeQuery(id+"F28.imprint","IMPRINT",EDGE,{"derivedFrom":sQuery(id+"F28.wireOp",EDGE,"E69.bottom")}),1.0]])]});
            extrude(context, id + "F29", {"entities" : qUnion([Q0]), "operationType" : NewBodyOperationType.REMOVE, "endBound" : BoundingType.UP_TO_NEXT, "oppositeDirection" : true, "depth" : 25 * mm});
        }
        {
            var Q0;
            Q0=makeQuery(id+"F5.boolean.opBoolean","COPY",FACE,{"derivedFrom":makeQuery(id+"F5.opExtrude","CAP_FACE",FACE,{"disambiguationData":[OSD([sQuery(id+"F4.wireOp",EDGE,"E19.bottom"),sQuery(id+"F4.wireOp",EDGE,"E19.top"),sQuery(id+"F4.wireOp",EDGE,"E19.left"),sQuery(id+"F4.wireOp",EDGE,"E19.right")])],"isStart":false})});
            var sketch = newSketch(context, id + "F30", { "sketchPlane" : qUnion([Q0])});
            skLineSegment(sketch, "E70", {"start": v(83.04, 49) * mm, "end": v(-54.72, 49) * mm, "construction": true});
            skLineSegment(sketch, "E71.bottom", {"start": v(-35, 54) * mm, "end": v(-50, 54) * mm});
            skLineSegment(sketch, "E71.top", {"start": v(-35, 44) * mm, "end": v(-50, 44) * mm});
            skLineSegment(sketch, "E71.left", {"start": v(-35, 54) * mm, "end": v(-35, 44) * mm});
            skLineSegment(sketch, "E71.right", {"start": v(-50, 54) * mm, "end": v(-50, 44) * mm});
            skSolve(sketch);
        }
        {
            var Q0;
            Q0 = qSketchRegion(id + "F30", true);
            var Q1;
            {var subQ1=sQuery(id+"F30.wireOp",EDGE,"DZUq5Ajw-Pgzt-FFcx-DODV-KdEy64VxGjmB.bottom");Q1=makeQuery(id+"F30.imprint","IMPRINT",FACE,{"disambiguationData":[TD([[makeQuery(id+"F30.imprint","IMPRINT",EDGE,{"derivedFrom":subQ1}),1.0]])]});}
            extrude(context, id + "F31", {"entities" : qUnion([Q0, Q1]), "operationType" : NewBodyOperationType.REMOVE, "oppositeDirection" : true, "depth" : 6 * mm});
        }
        {
            var Q0;
            Q0=makeQuery(id+"F15.opExtrude","CAP_FACE",FACE,{"disambiguationData":[OSD([sQuery(id+"F14.wireOp",EDGE,"E56.bottom"),sQuery(id+"F14.wireOp",EDGE,"E56.top"),sQuery(id+"F14.wireOp",EDGE,"E56.left"),sQuery(id+"F14.wireOp",EDGE,"E56.right")])],"isStart":false});
            var sketch = newSketch(context, id + "F32", { "sketchPlane" : qUnion([Q0])});
            skLineSegment(sketch, "E72.bottom", {"start": v(-9.95, 14.5) * mm, "end": v(-25.95, 14.5) * mm});
            skLineSegment(sketch, "E72.top", {"start": v(-9.95, 11.5) * mm, "end": v(-25.95, 11.5) * mm});
            skLineSegment(sketch, "E72.left", {"start": v(-9.95, 14.5) * mm, "end": v(-9.95, 11.5) * mm});
            skLineSegment(sketch, "E72.right", {"start": v(-25.95, 14.5) * mm, "end": v(-25.95, 11.5) * mm});
            skLineSegment(sketch, "E73", {"start": v(-7.95, 9.5) * mm, "end": v(-27.95, 9.5) * mm, "construction": true});
            skLineSegment(sketch, "E74", {"start": v(-17.95, 9.5) * mm, "end": v(-17.95, 15.6) * mm, "construction": true});
            skSolve(sketch);
        }
        {
            var Q0;
            Q0=makeQuery(id+"F32.imprint","IMPRINT",FACE,{"disambiguationData":[TD([[makeQuery(id+"F32.imprint","IMPRINT",EDGE,{"derivedFrom":sQuery(id+"F32.wireOp",EDGE,"E72.bottom")}),-1.0]])]});
            extrude(context, id + "F33", {"entities" : qUnion([Q0]), "operationType" : NewBodyOperationType.REMOVE, "oppositeDirection" : true, "depth" : 1 * mm});
        }
    });
